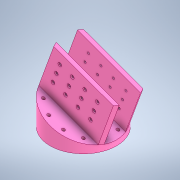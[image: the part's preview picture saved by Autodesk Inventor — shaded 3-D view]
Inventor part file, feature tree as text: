
AUTODESK INVENTOR PART (.ipt)
format: ipt  version: 2022.2 (Build 262287000, 287)  size: 287,232 bytes
history: native  units: mm
features: sketch x7, hole x4, extrude x3, pattern_linear x2, mirror x1
ambient origin geometry x8: Origin, YZ Plane, XZ Plane, XY Plane, X Axis, Y Axis, Z Axis, Center Point
bodies: Solid5 (feature_tree)
feature tree (17):
  extrude  "Extrusion31"  Depth=127.0mm
  sketch  "Sketch61"  dims[d335=10.0mm d336=0.0mm d337=3.490659mm]
  extrude  "Extrusion32"  Depth=10.0mm
  mirror  "Mirror4"
  sketch  "Sketch63"  dims[d340=8.0mm d341=40.64mm]
  sketch  "Sketch64"  dims[d342=107.95mm d343=45.0deg]
  hole  "Hole13"  [1 undecoded]
  extrude  "Extrusion33"  Depth=40.64mm
  hole  "Hole14"  [1 undecoded]
  hole  "Hole15"  [1 undecoded]
  pattern_linear  "Rectangular Pattern3"  Spacing1=0.0mm  [1 undecoded]
  hole  "Hole16"  [1 undecoded]
  pattern_linear  "Rectangular Pattern4"  Spacing1=19.05mm  [1 undecoded]
  sketch  "Sketch60"  dims[d233=76.2mm d334=127.0mm]
  sketch  "Sketch62"  dims[d338=8.0mm d339=0.0mm]
  sketch  "Sketch65"  dims[d344=120.0mm d346=360.0deg]
  sketch  "Sketch67"  dims[d348=5.613mm d349=6.0mm d350=9.779mm d351=2.0mm d352=14.3117mm d353=8.0mm d354=0.0mm d355=84.1375mm d356=0.0mm d357=6.3246mm d358=6.0mm d359=7.08914mm d360=7.40918mm d361=14.3117mm d362=9.525mm d363=0.0mm d364=19.05mm d365=19.05mm d366=4.305mm d367=6.0mm d368=7.087mm d369=2.362mm d370=14.3117mm d371=9.525mm d372=0.0mm d373=40.0mm d375=25.4mm d376=30.0mm d378=19.05mm d379=19.05mm d380=19.05mm d381=4.305mm d382=6.0mm d383=7.087mm d384=2.0mm d385=14.3117mm d386=8.0mm d387=0.0mm d388=40.0mm d390=25.4mm d391=30.0mm d393=19.05mm d64=1.0mm d65=1.0mm d66=1.0mm d67=0.15mm d68=0.25mm d69=0.375mm d70=14.3117mm d71=0.75mm d72=20.594885mm d73=0.0625mm d74=0.75mm d75=0.375mm]
note: 6 required parameter values undecoded (feature->parameter linkage not recoverable at this tier; creation-order binding heuristic only, values carry confidence <= 0.55)
